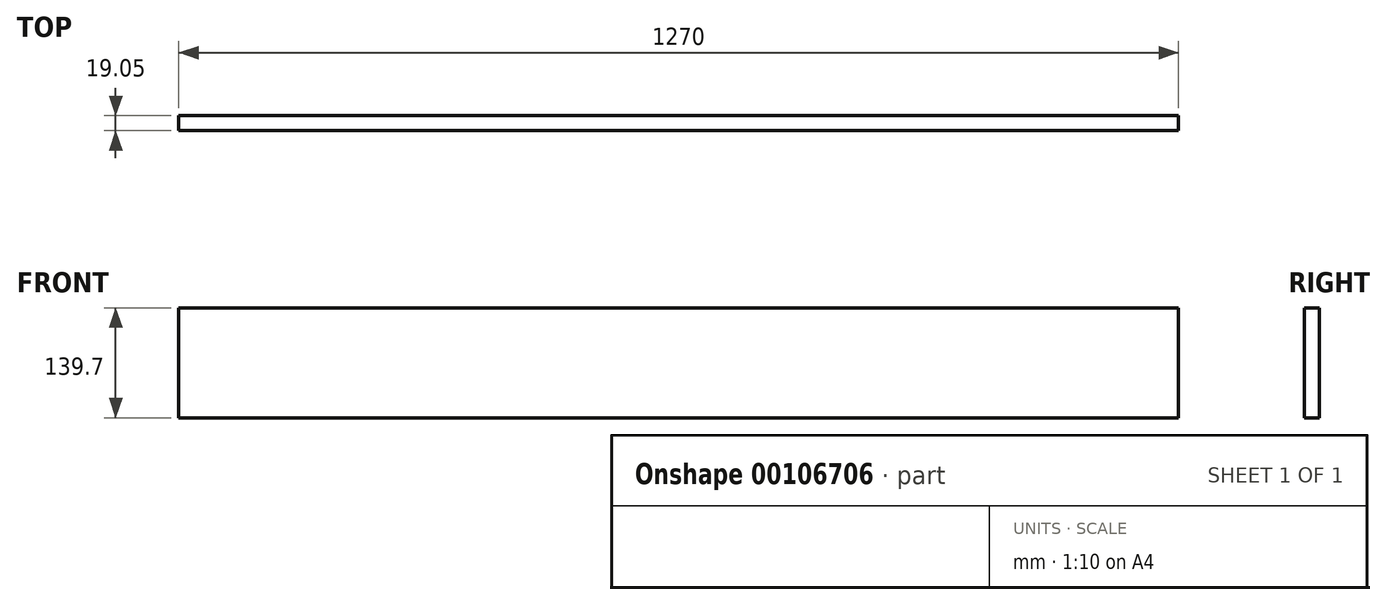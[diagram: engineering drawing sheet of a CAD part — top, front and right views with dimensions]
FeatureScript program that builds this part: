
annotation { "Feature Type Name" : "Feature", "Feature Type Description" : "" }
export const myFeature = defineFeature(function(context is Context, id is Id, definition is map)
    precondition{}
    {
        {
            var Q0;
            Q0=qCreatedBy(makeId("Front.planeOp"),FACE);
            var sketch = newSketch(context, id + "F0", { "sketchPlane" : qUnion([Q0])});
            skLineSegment(sketch, "E0.bottom", {"start": v(0, 0) * mm, "end": v(1270, 0) * mm});
            skLineSegment(sketch, "E0.top", {"start": v(0, 139.7) * mm, "end": v(1270, 139.7) * mm});
            skLineSegment(sketch, "E0.left", {"start": v(0, 0) * mm, "end": v(0, 139.7) * mm});
            skLineSegment(sketch, "E0.right", {"start": v(1270, 0) * mm, "end": v(1270, 139.7) * mm});
            skSolve(sketch);
        }
        {
            var Q0;
            Q0=makeQuery(id+"F0.imprint","IMPRINT",FACE,{"disambiguationData":[TD([[makeQuery(id+"F0.imprint","IMPRINT",EDGE,{"derivedFrom":sQuery(id+"F0.wireOp",EDGE,"E0.bottom")}),1.0]])]});
            extrude(context, id + "F1", {"entities" : qUnion([Q0]), "depth" : 19.05 * mm});
        }
    });
